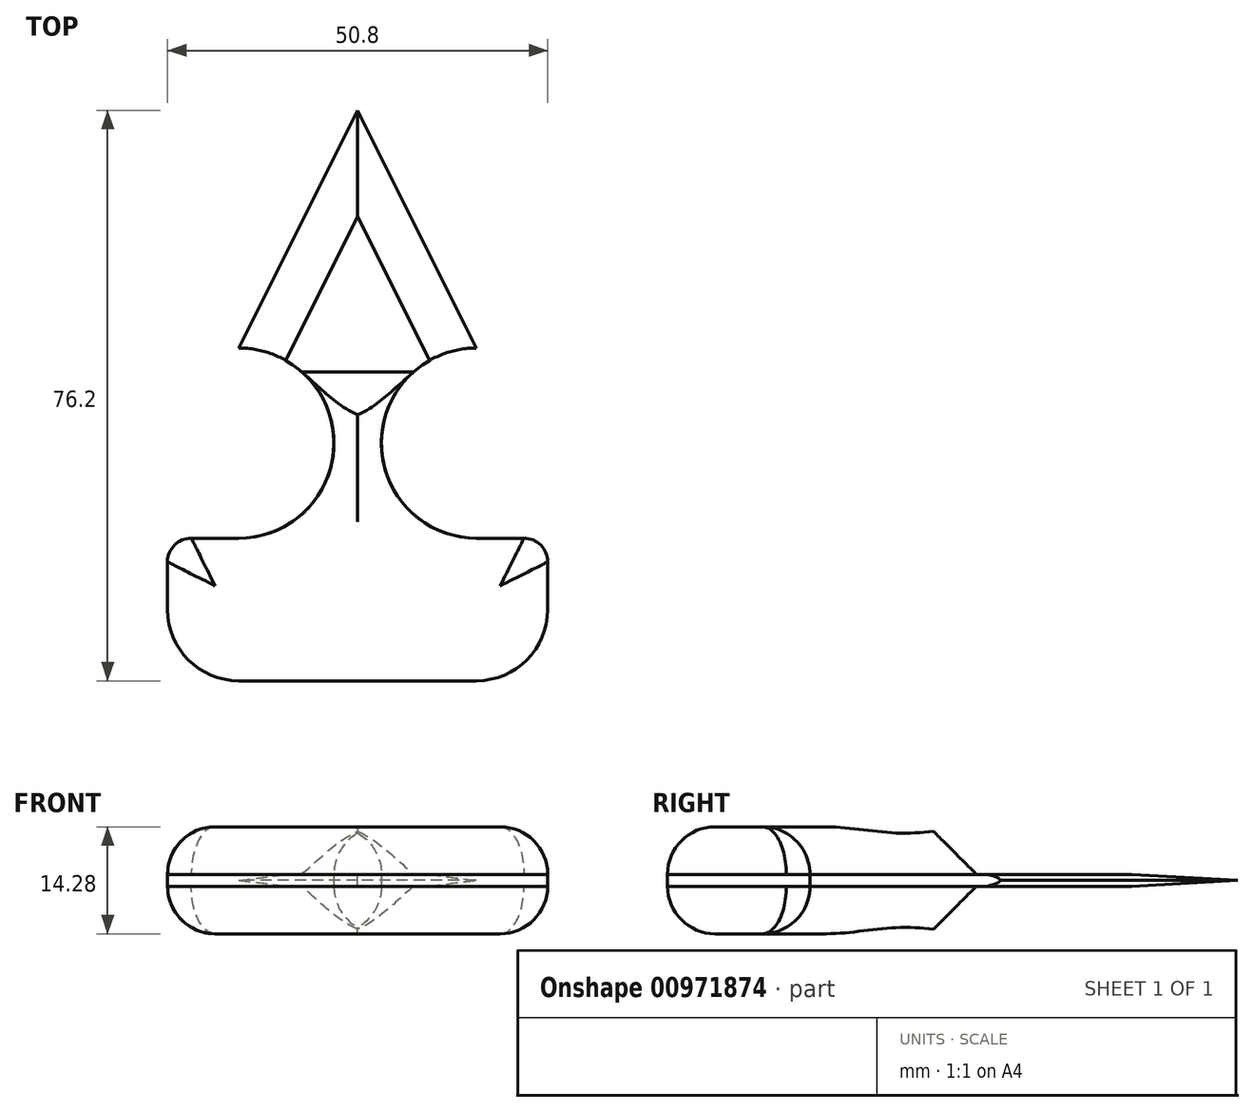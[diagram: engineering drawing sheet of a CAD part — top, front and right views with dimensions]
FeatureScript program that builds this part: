
annotation { "Feature Type Name" : "Feature", "Feature Type Description" : "" }
export const myFeature = defineFeature(function(context is Context, id is Id, definition is map)
    precondition{}
    {
        {
            var Q0;
            Q0=qCreatedBy(makeId("Top.planeOp"),FACE);
            var sketch = newSketch(context, id + "F0", { "sketchPlane" : qUnion([Q0])});
            skLineSegment(sketch, "E0.bottom", {"start": v(15.88, -38.1) * mm, "end": v(-15.87, -38.1) * mm});
            skLineSegment(sketch, "E0.top", {"start": v(25.4, 38.1) * mm, "end": v(-25.4, 38.1) * mm, "construction": true});
            skLineSegment(sketch, "E0.left", {"start": v(25.4, -28.57) * mm, "end": v(25.4, -22.23) * mm});
            skLineSegment(sketch, "E0.right", {"start": v(-25.4, -28.58) * mm, "end": v(-25.4, -22.23) * mm});
            skPoint(sketch, "E0.middle", {"position": v(0, 0) * mm});
            skLineSegment(sketch, "E1", {"start": v(-22.22, -19.05) * mm, "end": v(-15.88, -19.05) * mm});
            skLineSegment(sketch, "E2", {"start": v(-25.4, 6.35) * mm, "end": v(-15.88, 6.35) * mm, "construction": true});
            skArc(sketch, "E3", {"start": v(15.88, 6.35) * mm, "mid": v(3.18, -6.35) * mm, "end": v(15.88, -19.05) * mm});
            skArc(sketch, "E4", {"start": v(-15.88, -19.05) * mm, "mid": v(-3.18, -6.35) * mm, "end": v(-15.88, 6.35) * mm});
            skLineSegment(sketch, "E5.trimOffspring", {"start": v(15.88, 6.35) * mm, "end": v(25.4, 6.35) * mm, "construction": true});
            skLineSegment(sketch, "E6.trimOffspring", {"start": v(-25.4, 6.35) * mm, "end": v(-25.4, 38.1) * mm, "construction": true});
            skLineSegment(sketch, "E7.trimOffspring", {"start": v(25.4, 6.35) * mm, "end": v(25.4, 38.1) * mm, "construction": true});
            skPoint(sketch, "E8.visualSharp", {"position": v(25.4, -19.05) * mm});
            skArc(sketch, "E8.filletArc", {"start": v(25.4, -22.23) * mm, "mid": v(24.47, -19.98) * mm, "end": v(22.23, -19.05) * mm});
            skPoint(sketch, "E9.visualSharp", {"position": v(-25.4, -19.05) * mm});
            skArc(sketch, "E9.filletArc", {"start": v(-22.22, -19.05) * mm, "mid": v(-24.47, -19.98) * mm, "end": v(-25.4, -22.23) * mm});
            skPoint(sketch, "E10.visualSharp", {"position": v(25.4, -38.1) * mm});
            skArc(sketch, "E10.filletArc", {"start": v(15.88, -38.1) * mm, "mid": v(22.61, -35.31) * mm, "end": v(25.4, -28.57) * mm});
            skPoint(sketch, "E11.visualSharp", {"position": v(-25.4, -38.1) * mm});
            skArc(sketch, "E11.filletArc", {"start": v(-25.4, -28.58) * mm, "mid": v(-22.61, -35.31) * mm, "end": v(-15.87, -38.1) * mm});
            skLineSegment(sketch, "E12.trimOffspring", {"start": v(15.88, -19.05) * mm, "end": v(22.23, -19.05) * mm});
            skLineSegment(sketch, "E13", {"start": v(-15.88, 6.35) * mm, "end": v(0, 38.1) * mm});
            skLineSegment(sketch, "E14", {"start": v(0, 38.1) * mm, "end": v(15.88, 6.35) * mm});
            skSolve(sketch);
        }
        {
            var Q0;
            Q0 = qSketchRegion(id + "F0", true);
            extrude(context, id + "F1", {"entities" : qUnion([Q0]), "depth" : 0.8 * mm, "offsetDistance" : 25.4 * mm, "hasSecondDirection" : true, "secondDirectionOppositeDirection" : true, "secondDirectionDepth" : 0.8 * mm});
        }
        {
            var Q0;
            Q0=makeQuery(id+"F1.opExtrude","CAP_FACE",FACE,{"disambiguationData":[OSD([sQuery(id+"F0.wireOp",EDGE,"E0.bottom"),sQuery(id+"F0.wireOp",EDGE,"E0.left"),sQuery(id+"F0.wireOp",EDGE,"E0.right"),sQuery(id+"F0.wireOp",EDGE,"E1"),sQuery(id+"F0.wireOp",EDGE,"E3"),sQuery(id+"F0.wireOp",EDGE,"E4"),sQuery(id+"F0.wireOp",EDGE,"E8.filletArc"),sQuery(id+"F0.wireOp",EDGE,"E9.filletArc"),sQuery(id+"F0.wireOp",EDGE,"E10.filletArc"),sQuery(id+"F0.wireOp",EDGE,"E11.filletArc"),sQuery(id+"F0.wireOp",EDGE,"E12.trimOffspring"),sQuery(id+"F0.wireOp",EDGE,"E13"),sQuery(id+"F0.wireOp",EDGE,"E14")])],"isStart":false});
            var sketch = newSketch(context, id + "F2", { "sketchPlane" : qUnion([Q0])});
            skLineSegment(sketch, "E15", {"start": v(-7.47, 3.17) * mm, "end": v(7.47, 3.17) * mm});
            skSolve(sketch);
        }
        {
            var Q0;
            {var subQ2=sQuery(id+"F2.wireOp",EDGE,"E15");Q0=makeQuery(id+"F2.imprint","IMPRINT",FACE,{"disambiguationData":[TD([[makeQuery(id+"F2.imprint","IMPRINT",EDGE,{"derivedFrom":subQ2}),-1.0]])]});}
            extrude(context, id + "F3", {"entities" : qUnion([Q0]), "depth" : 6.35 * mm, "offsetDistance" : 25.4 * mm});
        }
        {
            var Q0;
            Q0=makeQuery(id+"F1.opExtrude","CAP_FACE",FACE,{"disambiguationData":[OSD([sQuery(id+"F0.wireOp",EDGE,"E0.bottom"),sQuery(id+"F0.wireOp",EDGE,"E0.left"),sQuery(id+"F0.wireOp",EDGE,"E0.right"),sQuery(id+"F0.wireOp",EDGE,"E1"),sQuery(id+"F0.wireOp",EDGE,"E3"),sQuery(id+"F0.wireOp",EDGE,"E4"),sQuery(id+"F0.wireOp",EDGE,"E8.filletArc"),sQuery(id+"F0.wireOp",EDGE,"E9.filletArc"),sQuery(id+"F0.wireOp",EDGE,"E10.filletArc"),sQuery(id+"F0.wireOp",EDGE,"E11.filletArc"),sQuery(id+"F0.wireOp",EDGE,"E12.trimOffspring"),sQuery(id+"F0.wireOp",EDGE,"E13"),sQuery(id+"F0.wireOp",EDGE,"E14")])],"isStart":true});
            var sketch = newSketch(context, id + "F4", { "sketchPlane" : qUnion([Q0])});
            skLineSegment(sketch, "E16", {"start": v(-7.47, -3.17) * mm, "end": v(7.47, -3.17) * mm});
            skSolve(sketch);
        }
        {
            var Q0;
            {var subQ2=sQuery(id+"F4.wireOp",EDGE,"E16");Q0=makeQuery(id+"F4.imprint","IMPRINT",FACE,{"disambiguationData":[TD([[makeQuery(id+"F4.imprint","IMPRINT",EDGE,{"derivedFrom":subQ2}),1.0]])]});}
            extrude(context, id + "F5", {"entities" : qUnion([Q0]), "depth" : 6.35 * mm, "offsetDistance" : 25.4 * mm});
        }
        {
            var Q0;
            Q0=makeQuery(id+"F5.opExtrude","CAP_EDGE",EDGE,{"disambiguationData":[OSD([sQuery(id+"F4.wireOp",EDGE,"E16")])],"isStart":false});
            var Q1;
            Q1=makeQuery(id+"F3.opExtrude","CAP_EDGE",EDGE,{"disambiguationData":[OSD([sQuery(id+"F2.wireOp",EDGE,"E15")])],"isStart":false});
            chamfer(context, id + "F6", {"entities" : qUnion([Q0, Q1]), "width" : 6.35 * mm, "tangentPropagation" : true});
        }
        {
            var Q0;
            Q0=makeQuery(id+"F3.opExtrude","CAP_EDGE",EDGE,{"disambiguationData":[OSD([sQuery(id+"F0.wireOp",EDGE,"E4")])],"isStart":false});
            var Q1;
            Q1=makeQuery(id+"F3.opExtrude","CAP_EDGE",EDGE,{"disambiguationData":[OSD([sQuery(id+"F0.wireOp",EDGE,"E1")])],"isStart":false});
            var Q2;
            Q2=makeQuery(id+"F3.opExtrude","CAP_EDGE",EDGE,{"disambiguationData":[OSD([sQuery(id+"F0.wireOp",EDGE,"E9.filletArc")])],"isStart":false});
            var Q3;
            Q3=makeQuery(id+"F3.opExtrude","CAP_EDGE",EDGE,{"disambiguationData":[OSD([sQuery(id+"F0.wireOp",EDGE,"E0.right")])],"isStart":false});
            var Q4;
            Q4=makeQuery(id+"F3.opExtrude","CAP_EDGE",EDGE,{"disambiguationData":[OSD([sQuery(id+"F0.wireOp",EDGE,"E11.filletArc")])],"isStart":false});
            var Q5;
            Q5=makeQuery(id+"F3.opExtrude","CAP_EDGE",EDGE,{"disambiguationData":[OSD([sQuery(id+"F0.wireOp",EDGE,"E0.bottom")])],"isStart":false});
            var Q6;
            Q6=makeQuery(id+"F3.opExtrude","CAP_EDGE",EDGE,{"disambiguationData":[OSD([sQuery(id+"F0.wireOp",EDGE,"E10.filletArc")])],"isStart":false});
            var Q7;
            Q7=makeQuery(id+"F3.opExtrude","CAP_EDGE",EDGE,{"disambiguationData":[OSD([sQuery(id+"F0.wireOp",EDGE,"E0.left")])],"isStart":false});
            var Q8;
            Q8=makeQuery(id+"F3.opExtrude","CAP_EDGE",EDGE,{"disambiguationData":[OSD([sQuery(id+"F0.wireOp",EDGE,"E8.filletArc")])],"isStart":false});
            var Q9;
            Q9=makeQuery(id+"F3.opExtrude","CAP_EDGE",EDGE,{"disambiguationData":[OSD([sQuery(id+"F0.wireOp",EDGE,"E12.trimOffspring")])],"isStart":false});
            var Q10;
            Q10=makeQuery(id+"F3.opExtrude","CAP_EDGE",EDGE,{"disambiguationData":[OSD([sQuery(id+"F0.wireOp",EDGE,"E3")])],"isStart":false});
            var Q11;
            Q11=makeQuery(id+"F5.opExtrude","CAP_EDGE",EDGE,{"disambiguationData":[OSD([sQuery(id+"F0.wireOp",EDGE,"E4")])],"isStart":false});
            var Q12;
            Q12=makeQuery(id+"F5.opExtrude","CAP_EDGE",EDGE,{"disambiguationData":[OSD([sQuery(id+"F0.wireOp",EDGE,"E1")])],"isStart":false});
            var Q13;
            Q13=makeQuery(id+"F5.opExtrude","CAP_EDGE",EDGE,{"disambiguationData":[OSD([sQuery(id+"F0.wireOp",EDGE,"E9.filletArc")])],"isStart":false});
            var Q14;
            Q14=makeQuery(id+"F5.opExtrude","CAP_EDGE",EDGE,{"disambiguationData":[OSD([sQuery(id+"F0.wireOp",EDGE,"E0.right")])],"isStart":false});
            var Q15;
            Q15=makeQuery(id+"F5.opExtrude","CAP_EDGE",EDGE,{"disambiguationData":[OSD([sQuery(id+"F0.wireOp",EDGE,"E11.filletArc")])],"isStart":false});
            var Q16;
            Q16=makeQuery(id+"F5.opExtrude","CAP_EDGE",EDGE,{"disambiguationData":[OSD([sQuery(id+"F0.wireOp",EDGE,"E0.bottom")])],"isStart":false});
            var Q17;
            Q17=makeQuery(id+"F5.opExtrude","CAP_EDGE",EDGE,{"disambiguationData":[OSD([sQuery(id+"F0.wireOp",EDGE,"E3")])],"isStart":false});
            var Q18;
            Q18=makeQuery(id+"F5.opExtrude","CAP_EDGE",EDGE,{"disambiguationData":[OSD([sQuery(id+"F0.wireOp",EDGE,"E12.trimOffspring")])],"isStart":false});
            var Q19;
            Q19=makeQuery(id+"F5.opExtrude","CAP_EDGE",EDGE,{"disambiguationData":[OSD([sQuery(id+"F0.wireOp",EDGE,"E8.filletArc")])],"isStart":false});
            var Q20;
            Q20=makeQuery(id+"F5.opExtrude","CAP_EDGE",EDGE,{"disambiguationData":[OSD([sQuery(id+"F0.wireOp",EDGE,"E0.left")])],"isStart":false});
            var Q21;
            Q21=makeQuery(id+"F5.opExtrude","CAP_EDGE",EDGE,{"disambiguationData":[OSD([sQuery(id+"F0.wireOp",EDGE,"E10.filletArc")])],"isStart":false});
            fillet(context, id + "F7", {"entities" : qUnion([Q0, Q1, Q2, Q3, Q4, Q5, Q6, Q7, Q8, Q9, Q10, Q11, Q12, Q13, Q14, Q15, Q16, Q17, Q18, Q19, Q20, Q21]), "radius" : 6.35 * mm, "tangentPropagation" : true, "allowEdgeOverflow" : false});
        }
        {
            var Q0;
            Q0=makeQuery(id+"F1.opExtrude","CAP_EDGE",EDGE,{"disambiguationData":[OSD([sQuery(id+"F0.wireOp",EDGE,"E14")])],"isStart":true});
            var Q1;
            Q1=makeQuery(id+"F1.opExtrude","CAP_EDGE",EDGE,{"disambiguationData":[OSD([sQuery(id+"F0.wireOp",EDGE,"E13")])],"isStart":true});
            chamfer(context, id + "F8", {"entities" : qUnion([Q0, Q1]), "chamferType" : ChamferType.TWO_OFFSETS, "width1" : 0.8 * mm, "oppositeDirection" : true, "width2" : 6.35 * mm, "tangentPropagation" : true});
        }
        {
            var Q0;
            {var subQ0=sQuery(id+"F0.wireOp",EDGE,"E0.bottom");Q0=makeQuery(id+"F7.opFillet","BLEND_EDGE",EDGE,{"blendedFrom":[makeQuery(id+"F5.opExtrude","CAP_EDGE",EDGE,{"disambiguationData":[OSD([subQ0])],"isStart":false}),makeQuery(id+"F5.opExtrude","CAP_FACE",FACE,{"disambiguationData":[OSD([subQ0,sQuery(id+"F0.wireOp",EDGE,"E0.left"),sQuery(id+"F0.wireOp",EDGE,"E0.right"),sQuery(id+"F0.wireOp",EDGE,"E1"),sQuery(id+"F0.wireOp",EDGE,"E3"),sQuery(id+"F0.wireOp",EDGE,"E4"),sQuery(id+"F0.wireOp",EDGE,"E8.filletArc"),sQuery(id+"F0.wireOp",EDGE,"E9.filletArc"),sQuery(id+"F0.wireOp",EDGE,"E10.filletArc"),sQuery(id+"F0.wireOp",EDGE,"E11.filletArc"),sQuery(id+"F0.wireOp",EDGE,"E12.trimOffspring"),sQuery(id+"F4.wireOp",EDGE,"E16")])],"isStart":false})],"blendedInto":[makeQuery(id+"F5.opExtrude","CAP_FACE",FACE,{"disambiguationData":[OSD([subQ0,sQuery(id+"F0.wireOp",EDGE,"E0.left"),sQuery(id+"F0.wireOp",EDGE,"E0.right"),sQuery(id+"F0.wireOp",EDGE,"E1"),sQuery(id+"F0.wireOp",EDGE,"E3"),sQuery(id+"F0.wireOp",EDGE,"E4"),sQuery(id+"F0.wireOp",EDGE,"E8.filletArc"),sQuery(id+"F0.wireOp",EDGE,"E9.filletArc"),sQuery(id+"F0.wireOp",EDGE,"E10.filletArc"),sQuery(id+"F0.wireOp",EDGE,"E11.filletArc"),sQuery(id+"F0.wireOp",EDGE,"E12.trimOffspring"),sQuery(id+"F4.wireOp",EDGE,"E16")])],"isStart":false})]});}
            var Q1;
            Q1=makeQuery(id+"F1.opExtrude","CAP_EDGE",EDGE,{"disambiguationData":[OSD([sQuery(id+"F0.wireOp",EDGE,"E14")])],"isStart":false});
            var Q2;
            Q2=makeQuery(id+"F1.opExtrude","CAP_EDGE",EDGE,{"disambiguationData":[OSD([sQuery(id+"F0.wireOp",EDGE,"E13")])],"isStart":false});
            chamfer(context, id + "F9", {"entities" : qUnion([Q0, Q1, Q2]), "chamferType" : ChamferType.TWO_OFFSETS, "width1" : 0.8 * mm, "oppositeDirection" : false, "width2" : 6.35 * mm, "tangentPropagation" : true});
        }
    });
